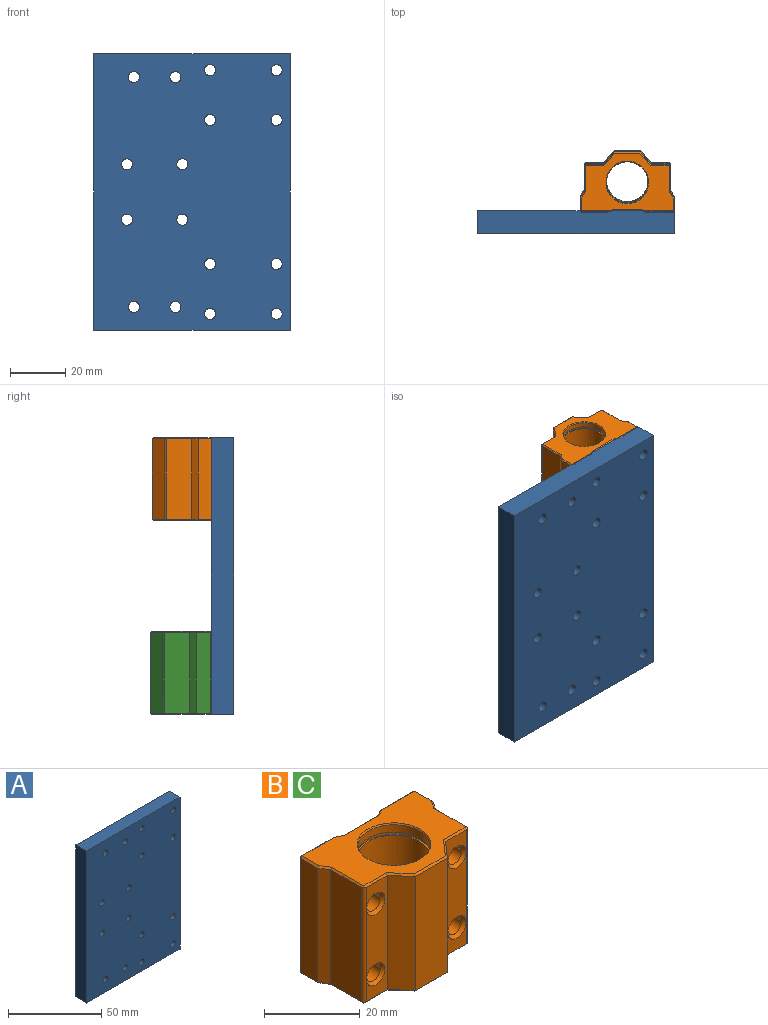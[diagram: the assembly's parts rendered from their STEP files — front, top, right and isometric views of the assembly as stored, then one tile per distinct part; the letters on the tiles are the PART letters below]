
ASSEMBLY  parts=3 mates=2
PART A: 22 faces, bbox 71x8x100 mm
  f0: plane 71.05x8mm, normal (0,0,-1), area 568.4mm2, adj f1,f19,f20,f21
  f1: plane 100x8mm, normal (1,0,0), area 800mm2, adj f0,f2,f20,f21
  f2: plane 71.05x8mm, normal (0,0,1), area 568.4mm2, adj f1,f19,f20,f21
  f3: cylinder r=2mm len=8mm, axis (0,1,0), area 100.5mm2, adj f20,f21
  f4: cylinder r=2mm len=8mm, axis (0,1,0), area 100.5mm2, adj f20,f21
  f5: cylinder r=2mm len=8mm, axis (0,1,0), area 100.5mm2, adj f20,f21
  f6: cylinder r=2mm len=8mm, axis (0,1,0), area 100.5mm2, adj f20,f21
  f7: cylinder r=2mm len=8mm, axis (0,1,0), area 100.5mm2, adj f20,f21
  f8: cylinder r=2mm len=8mm, axis (0,1,0), area 100.5mm2, adj f20,f21
  f9: cylinder r=2mm len=8mm, axis (0,1,0), area 100.5mm2, adj f20,f21
  f10: cylinder r=2mm len=8mm, axis (0,1,0), area 100.5mm2, adj f20,f21
  f11: cylinder r=2mm len=8mm, axis (0,1,0), area 100.5mm2, adj f20,f21
  f12: cylinder r=2mm len=8mm, axis (0,1,0), area 100.5mm2, adj f20,f21
  f13: cylinder r=2mm len=8mm, axis (0,1,0), area 100.5mm2, adj f20,f21
  f14: cylinder r=2mm len=8mm, axis (0,1,0), area 100.5mm2, adj f20,f21
  f15: cylinder r=2mm len=8mm, axis (0,1,0), area 100.5mm2, adj f20,f21
  f16: cylinder r=2mm len=8mm, axis (0,1,0), area 100.5mm2, adj f20,f21
  f17: cylinder r=2mm len=8mm, axis (0,1,0), area 100.5mm2, adj f20,f21
  f18: cylinder r=2mm len=8mm, axis (0,1,0), area 100.5mm2, adj f20,f21
  f19: plane 100x8mm, normal (-1,0,0), area 800mm2, adj f0,f2,f20,f21
  f20: plane 100x71.05mm, normal (0,-1,0), area 6903.5mm2, adj f0,f1,f2,f3,f4,f5,f6,f7
  f21: plane 100x71.05mm, normal (0,1,0), area 6903.5mm2, adj f0,f1,f2,f3,f4,f5,f6,f7
PART B: 81 faces, bbox 34x22x30 mm
  f0: cylinder r=7.5mm len=24mm, axis (0,0,-1), area 1131mm2, adj f76,f79
  f1: cylinder r=7.5mm len=15mm, axis (0,0,-1), area 94.2mm2, adj f21,f80
  f2: plane 33.2x21.2mm, normal (0,0,1), area 384.4mm2, adj f22,f39,f42,f43,f48,f49,f53,f54
  f3: plane 33.2x21.2mm, normal (0,0,-1), area 377.3mm2, adj f21,f35,f36,f37,f38,f40,f41,f44
  f4: plane 29.2x2mm, normal (-0.45,0.89,0), area 65.3mm2, adj f5,f19,f56,f71
  f5: plane 29.2x10mm, normal (0,1,0), area 292mm2, adj f4,f6,f51,f69
  f6: plane 29.2x2mm, normal (0.45,0.89,0), area 65.3mm2, adj f5,f7,f46,f66
  f7: plane 29.2x9.6mm, normal (0,1,0), area 234.5mm2, adj f6,f32,f34,f45,f55,f63
  f8: plane 29.2x5.1mm, normal (-1,0,0), area 148.9mm2, adj f9,f44,f54,f55
  f9: plane 29.2x2.3mm, normal (-0.84,-0.55,0), area 80.2mm2, adj f8,f10,f40,f49
  f10: plane 29.2x9.1mm, normal (-1,0,0), area 265.7mm2, adj f9,f37,f43,f74
  f11: plane 29.2x6.2mm, normal (0,-1,0), area 135.2mm2, adj f12,f27,f28,f35,f39,f74
  f12: plane 29.2x4.4mm, normal (-0.75,-0.66,0), area 170.7mm2, adj f11,f13,f36,f42
  f13: plane 29.2x9.5mm, normal (0,-1,0), area 277.4mm2, adj f12,f14,f38,f48
  f14: plane 29.2x4.4mm, normal (0.75,-0.66,0), area 170.7mm2, adj f13,f15,f41,f53
  f15: plane 29.2x6.2mm, normal (0,-1,0), area 135.2mm2, adj f14,f29,f30,f47,f58,f73
  f16: plane 29.2x9.1mm, normal (1,0,0), area 265.7mm2, adj f17,f52,f62,f73
  f17: plane 29.2x2.3mm, normal (0.84,-0.55,0), area 80.2mm2, adj f16,f18,f57,f65
  f18: plane 29.2x5.1mm, normal (1,0,0), area 148.9mm2, adj f17,f61,f67,f68
  f19: plane 29.2x9.6mm, normal (0,1,0), area 234.5mm2, adj f4,f31,f33,f60,f67,f72
  f20: cylinder r=7.5mm len=15mm, axis (0,0,-1), area 87.3mm2, adj f22,f77
  f21: cone r=7.85mm half-angle=60deg, axis (0,0,-1), area 19.3mm2, adj f1,f3
  f22: cone r=7.5mm half-angle=30deg, axis (0,0,1), area 19.1mm2, adj f2,f20
  f23: cylinder r=2mm len=16.2mm, axis (0,1,0), area 203.6mm2, adj f28,f34
  f24: cylinder r=2mm len=16.2mm, axis (0,1,0), area 203.6mm2, adj f30,f33
  f25: cylinder r=2mm len=16.2mm, axis (0,1,0), area 203.6mm2, adj f27,f32
  f26: cylinder r=2mm len=16.2mm, axis (0,1,0), area 203.6mm2, adj f29,f31
  f27: cone r=2.7mm half-angle=45deg, axis (0,-1,0), area 14.6mm2, adj f11,f25
  f28: cone r=2.7mm half-angle=45deg, axis (0,-1,0), area 14.6mm2, adj f11,f23
  f29: cone r=2.7mm half-angle=45deg, axis (0,-1,0), area 14.6mm2, adj f15,f26
  f30: cone r=2.7mm half-angle=45deg, axis (0,-1,0), area 14.6mm2, adj f15,f24
  f31: cone r=2mm half-angle=45deg, axis (0,1,0), area 14.6mm2, adj f19,f26
  f32: cone r=2mm half-angle=45deg, axis (0,1,0), area 14.6mm2, adj f7,f25
  f33: cone r=2mm half-angle=45deg, axis (0,1,0), area 14.6mm2, adj f19,f24
  f34: cone r=2mm half-angle=45deg, axis (0,1,0), area 14.6mm2, adj f7,f23
  f35: plane 6.88x0.4mm, normal (0,-0.71,-0.71), area 3.8mm2, adj f3,f11,f36,f37,f74
  f36: plane 4.8x4.03mm, normal (-0.53,-0.47,-0.71), area 3.3mm2, adj f3,f12,f35,f38
  f37: plane 9.71x0.4mm, normal (-0.71,0,-0.71), area 5.4mm2, adj f3,f10,f35,f40,f74
  f38: plane 9.5x0.4mm, normal (0,-0.71,-0.71), area 5.3mm2, adj f3,f13,f36,f41
  f39: plane 6.88x0.4mm, normal (0,-0.71,0.71), area 3.8mm2, adj f2,f11,f42,f43,f74
  f40: plane 2.42x1.9mm, normal (-0.59,-0.39,-0.71), area 1.6mm2, adj f3,f9,f37,f44
  f41: plane 4.8x4.03mm, normal (0.53,-0.47,-0.71), area 3.3mm2, adj f3,f14,f38,f47
  f42: plane 4.8x4.03mm, normal (-0.53,-0.47,0.71), area 3.3mm2, adj f2,f12,f39,f48
  f43: plane 9.71x0.4mm, normal (-0.71,0,0.71), area 5.4mm2, adj f2,f10,f39,f49,f74
  f44: plane 5.1x0.4mm, normal (-0.71,0,-0.71), area 2.9mm2, adj f3,f8,f40,f50
  f45: plane 9.6x0.4mm, normal (0,0.71,-0.71), area 5.4mm2, adj f3,f7,f46,f50
  f46: plane 2.09x1.4mm, normal (0.32,0.63,-0.71), area 1.3mm2, adj f3,f6,f45,f51
  f47: plane 6.88x0.4mm, normal (0,-0.71,-0.71), area 3.8mm2, adj f3,f15,f41,f52,f73
  f48: plane 9.5x0.4mm, normal (0,-0.71,0.71), area 5.3mm2, adj f2,f13,f42,f53
  f49: plane 2.42x1.9mm, normal (-0.59,-0.39,0.71), area 1.6mm2, adj f2,f9,f43,f54
  f50: plane 0.4x0.4mm, normal (-0.58,0.58,-0.58), area 0.1mm2, adj f44,f45,f55
  f51: plane 10.19x0.4mm, normal (0,0.71,-0.71), area 5.7mm2, adj f3,f5,f46,f56
  f52: plane 9.71x0.4mm, normal (0.71,0,-0.71), area 5.4mm2, adj f3,f16,f47,f57,f73
  f53: plane 4.8x4.03mm, normal (0.53,-0.47,0.71), area 3.3mm2, adj f2,f14,f48,f58
  f54: plane 5.1x0.4mm, normal (-0.71,0,0.71), area 2.9mm2, adj f2,f8,f49,f59
  f55: plane 29.2x0.4mm, normal (-0.71,0.71,0), area 16.5mm2, adj f7,f8,f50,f59
  f56: plane 2.09x1.4mm, normal (-0.32,0.63,-0.71), area 1.3mm2, adj f3,f4,f51,f60
  f57: plane 2.42x1.9mm, normal (0.59,-0.39,-0.71), area 1.6mm2, adj f3,f17,f52,f61
  f58: plane 6.88x0.4mm, normal (0,-0.71,0.71), area 3.8mm2, adj f2,f15,f53,f62,f73
  f59: plane 0.4x0.4mm, normal (-0.58,0.58,0.58), area 0.1mm2, adj f54,f55,f63
  f60: plane 9.6x0.4mm, normal (0,0.71,-0.71), area 5.4mm2, adj f3,f19,f56,f64
  f61: plane 5.1x0.4mm, normal (0.71,0,-0.71), area 2.9mm2, adj f3,f18,f57,f64
  f62: plane 9.71x0.4mm, normal (0.71,0,0.71), area 5.4mm2, adj f2,f16,f58,f65,f73
  f63: plane 9.6x0.4mm, normal (0,0.71,0.71), area 5.4mm2, adj f2,f7,f59,f66
  f64: plane 0.4x0.4mm, normal (0.58,0.58,-0.58), area 0.1mm2, adj f60,f61,f67
  f65: plane 2.42x1.9mm, normal (0.59,-0.39,0.71), area 1.6mm2, adj f2,f17,f62,f68
  f66: plane 2.09x1.4mm, normal (0.32,0.63,0.71), area 1.3mm2, adj f2,f6,f63,f69
  f67: plane 29.2x0.4mm, normal (0.71,0.71,0), area 16.5mm2, adj f18,f19,f64,f70
  f68: plane 5.1x0.4mm, normal (0.71,0,0.71), area 2.9mm2, adj f2,f18,f65,f70
  f69: plane 10.19x0.4mm, normal (0,0.71,0.71), area 5.7mm2, adj f2,f5,f66,f71
  f70: plane 0.4x0.4mm, normal (0.58,0.58,0.58), area 0.1mm2, adj f67,f68,f72
  f71: plane 2.09x1.4mm, normal (-0.32,0.63,0.71), area 1.3mm2, adj f2,f4,f69,f72
  f72: plane 9.6x0.4mm, normal (0,0.71,0.71), area 5.4mm2, adj f2,f19,f70,f71
  f73: cylinder r=0.7mm len=29.61mm, axis (0,0,-1), area 32.3mm2, adj f15,f16,f47,f52,f58,f62
  f74: cylinder r=0.7mm len=29.61mm, axis (0,0,-1), area 32.3mm2, adj f10,f11,f35,f37,f39,f43
  f75: cylinder r=7.83mm len=15.66mm, axis (0,0,1), area 39.4mm2, adj f76,f77
  f76: plane 15.66x15.66mm, normal (0,0,1), area 15.9mm2, adj f0,f75
  f77: plane 15.66x15.66mm, normal (0,0,-1), area 15.9mm2, adj f20,f75
  f78: cylinder r=7.83mm len=15.66mm, axis (0,0,-1), area 39.4mm2, adj f79,f80
  f79: plane 15.66x15.66mm, normal (0,0,-1), area 15.9mm2, adj f0,f78
  f80: plane 15.66x15.66mm, normal (0,0,1), area 15.9mm2, adj f1,f78
PART C: same geometry as B
PLACE A t=(-11.44,1.21,-0.33)mm fixed
PLACE B rot(axis=(0,0,1),180deg) t=(14.06,0.51,34.67)mm
PLACE C rot(axis=(0,0,1),180deg) t=(14.06,1.21,-35.33)mm
MATE fastened B.f27 <-> A.f3  axis (0,1,0) through (26.06,1.21,43.67)mm
MATE fastened C.f27 <-> A.f10  axis (0,-1,0) through (26.06,1.21,-26.33)mm
